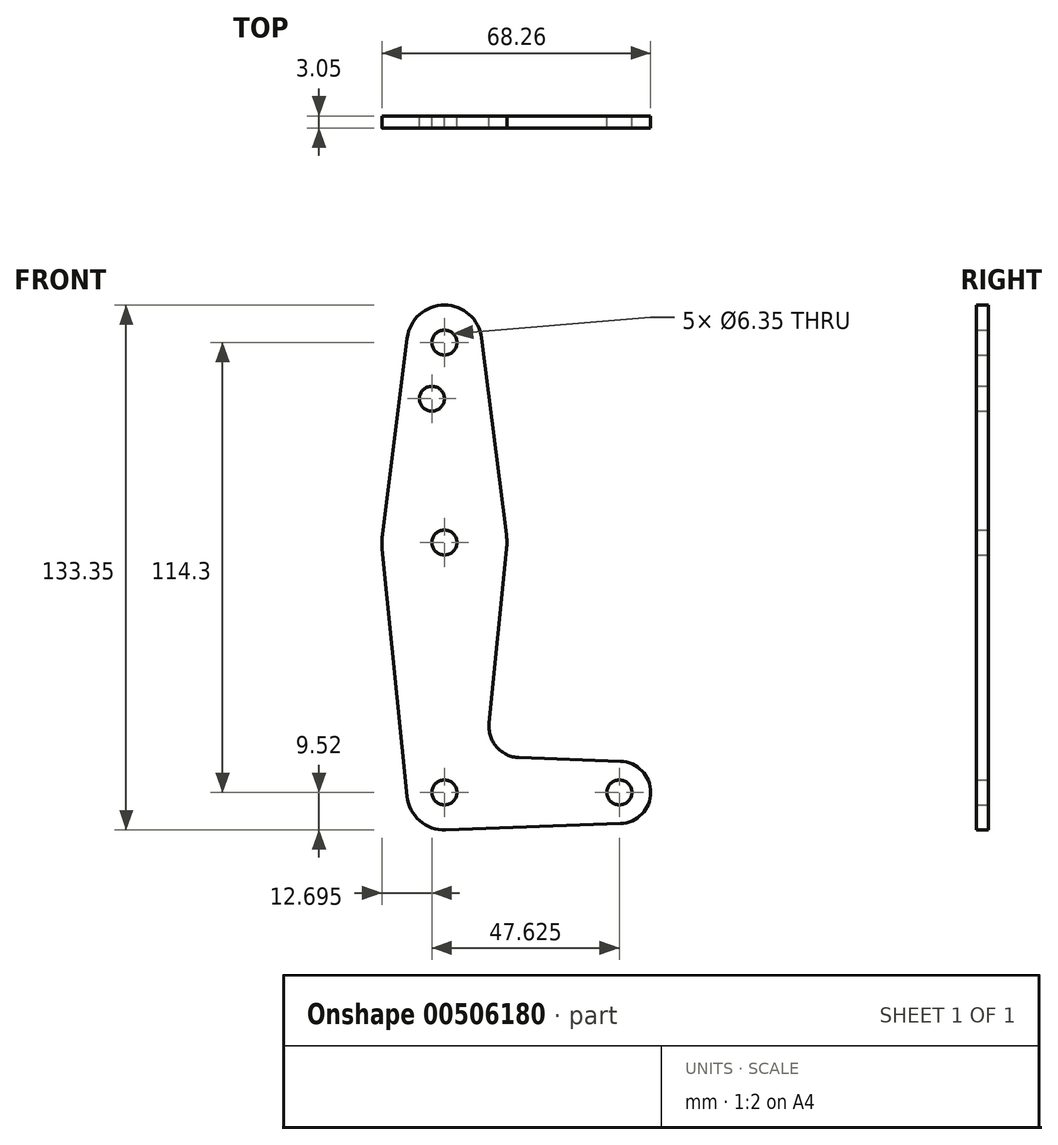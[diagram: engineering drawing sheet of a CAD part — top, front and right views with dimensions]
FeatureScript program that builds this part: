
annotation { "Feature Type Name" : "Feature", "Feature Type Description" : "" }
export const myFeature = defineFeature(function(context is Context, id is Id, definition is map)
    precondition{}
    {
        {
            var Q0;
            Q0=qCreatedBy(makeId("Front.planeOp"),FACE);
            var sketch = newSketch(context, id + "F0", { "sketchPlane" : qUnion([Q0])});
            skLineSegment(sketch, "E0", {"start": v(0, 0) * mm, "end": v(0, 63.5) * mm, "construction": true});
            skLineSegment(sketch, "E1", {"start": v(0, 63.5) * mm, "end": v(0, 114.3) * mm, "construction": true});
            skLineSegment(sketch, "E2", {"start": v(0, 0) * mm, "end": v(44.45, 0) * mm, "construction": true});
            skCircle(sketch, "E3", {"center": v(0, 114.3) * mm, "radius": 9.53 * mm});
            skCircle(sketch, "E4", {"center": v(0, 63.5) * mm, "radius": 15.88 * mm});
            skCircle(sketch, "E5", {"center": v(0, 0) * mm, "radius": 9.53 * mm});
            skCircle(sketch, "E6", {"center": v(44.45, 0) * mm, "radius": 7.94 * mm});
            skLineSegment(sketch, "E7", {"start": v(9.45, 115.5) * mm, "end": v(15.75, 65.48) * mm});
            skLineSegment(sketch, "E8", {"start": v(-9.45, 115.5) * mm, "end": v(-15.75, 65.48) * mm});
            skLineSegment(sketch, "E9", {"start": v(18.97, 8.85) * mm, "end": v(44.73, 7.93) * mm});
            skLineSegment(sketch, "E10", {"start": v(0.34, -9.52) * mm, "end": v(44.73, -7.93) * mm});
            skLineSegment(sketch, "E11", {"start": v(-15.8, 61.91) * mm, "end": v(-9.48, -0.95) * mm});
            skLineSegment(sketch, "E12", {"start": v(15.8, 61.91) * mm, "end": v(11.34, 17.6) * mm});
            skCircle(sketch, "E13", {"center": v(0, 114.3) * mm, "radius": 3.18 * mm});
            skCircle(sketch, "E14", {"center": v(0, 63.5) * mm, "radius": 3.18 * mm});
            skCircle(sketch, "E15", {"center": v(0, 0) * mm, "radius": 3.18 * mm});
            skCircle(sketch, "E16", {"center": v(44.45, 0) * mm, "radius": 3.18 * mm});
            skCircle(sketch, "E17", {"center": v(-3.17, 100.03) * mm, "radius": 3.18 * mm});
            skArc(sketch, "E18.filletArc", {"start": v(11.34, 17.6) * mm, "mid": v(13.26, 11.57) * mm, "end": v(18.97, 8.85) * mm});
            skSolve(sketch);
        }
        {
            var Q0;
            Q0=makeQuery(id+"F0.imprint","IMPRINT",FACE,{"disambiguationData":[TD([[makeQuery(id+"F0.imprint","IMPRINT",EDGE,{"derivedFrom":sQuery(id+"F0.wireOp",EDGE,"E13")}),-1.0]])]});
            var Q1;
            {var subQ0=sQuery(id+"F0.wireOp",EDGE,"E7");Q1=makeQuery(id+"F0.imprint","IMPRINT",FACE,{"disambiguationData":[TD([[makeQuery(id+"F0.imprint","IMPRINT",EDGE,{"derivedFrom":subQ0}),-1.0]])]});}
            var Q2;
            Q2=makeQuery(id+"F0.imprint","IMPRINT",FACE,{"disambiguationData":[TD([[makeQuery(id+"F0.imprint","IMPRINT",EDGE,{"derivedFrom":sQuery(id+"F0.wireOp",EDGE,"E14")}),-1.0]])]});
            var Q3;
            {var subQ0=sQuery(id+"F0.wireOp",EDGE,"E9");Q3=makeQuery(id+"F0.imprint","IMPRINT",FACE,{"disambiguationData":[TD([[makeQuery(id+"F0.imprint","IMPRINT",EDGE,{"derivedFrom":subQ0}),-1.0]])]});}
            var Q4;
            Q4=makeQuery(id+"F0.imprint","IMPRINT",FACE,{"disambiguationData":[TD([[makeQuery(id+"F0.imprint","IMPRINT",EDGE,{"derivedFrom":sQuery(id+"F0.wireOp",EDGE,"E15")}),-1.0]])]});
            var Q5;
            Q5=makeQuery(id+"F0.imprint","IMPRINT",FACE,{"disambiguationData":[TD([[makeQuery(id+"F0.imprint","IMPRINT",EDGE,{"derivedFrom":sQuery(id+"F0.wireOp",EDGE,"E16")}),-1.0]])]});
            extrude(context, id + "F1", {"entities" : qUnion([Q0, Q1, Q2, Q3, Q4, Q5]), "depth" : 3.05 * mm});
        }
    });
